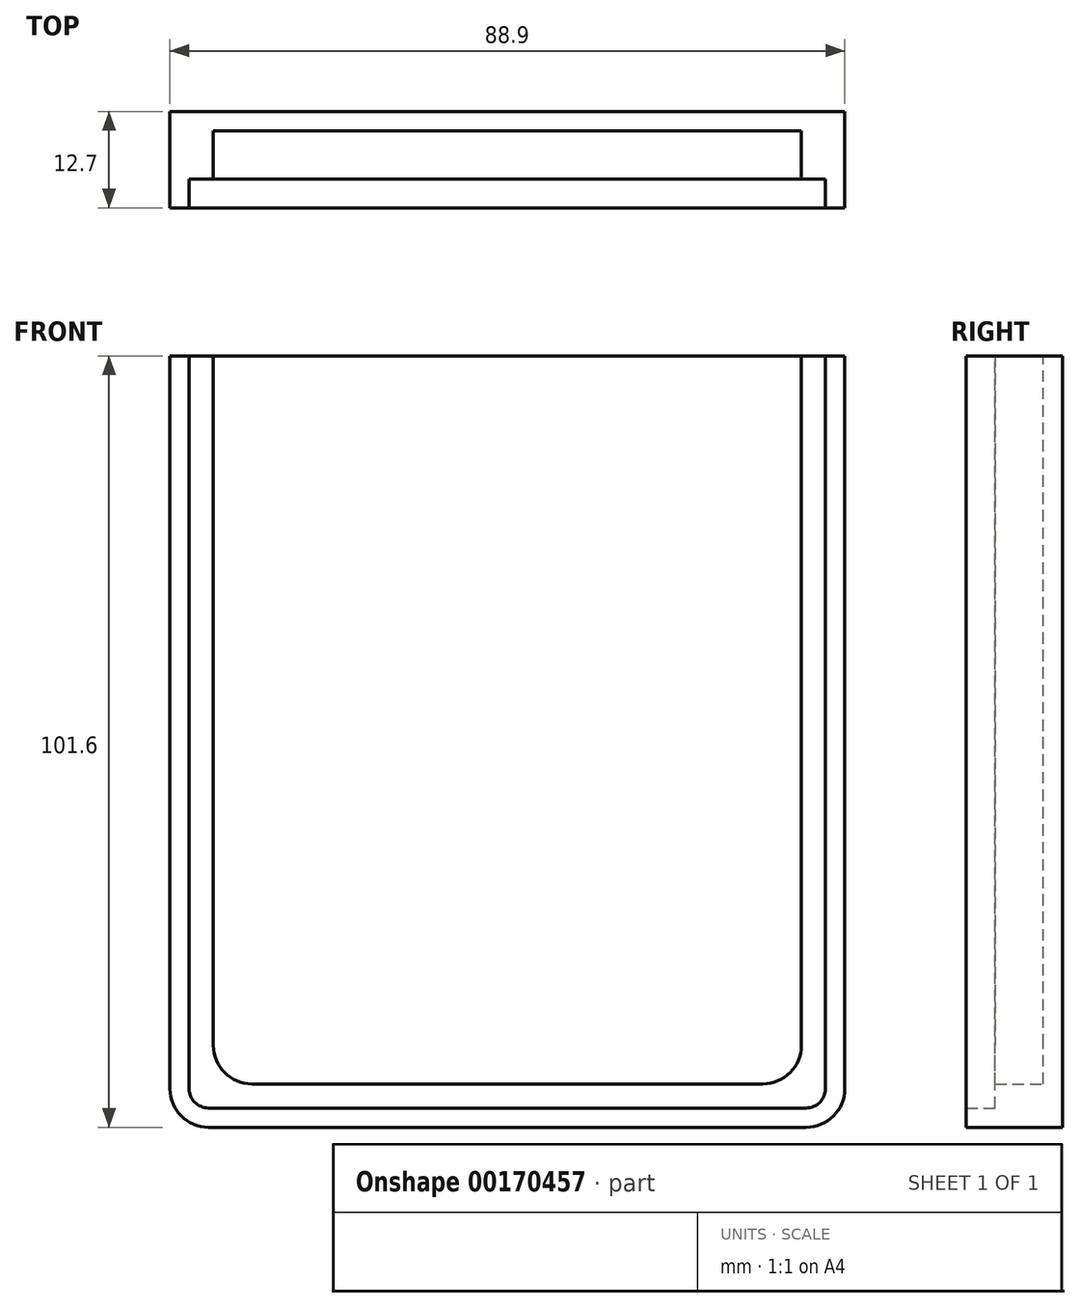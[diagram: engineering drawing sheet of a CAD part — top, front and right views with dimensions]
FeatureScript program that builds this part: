
annotation { "Feature Type Name" : "Feature", "Feature Type Description" : "" }
export const myFeature = defineFeature(function(context is Context, id is Id, definition is map)
    precondition{}
    {
        {
            var Q0;
            Q0=qCreatedBy(makeId("Front.planeOp"),FACE);
            var sketch = newSketch(context, id + "F0", { "sketchPlane" : qUnion([Q0])});
            skLineSegment(sketch, "E0.bottom", {"start": v(44.45, 0) * mm, "end": v(-44.45, 0) * mm});
            skLineSegment(sketch, "E0.top", {"start": v(44.45, 101.6) * mm, "end": v(-44.45, 101.6) * mm});
            skLineSegment(sketch, "E0.left", {"start": v(44.45, 0) * mm, "end": v(44.45, 101.6) * mm});
            skLineSegment(sketch, "E0.right", {"start": v(-44.45, 0) * mm, "end": v(-44.45, 101.6) * mm});
            skPoint(sketch, "E0.middle", {"position": v(0, 50.8) * mm});
            skLineSegment(sketch, "E1", {"start": v(0, 50.8) * mm, "end": v(0, 0) * mm, "construction": true});
            skSolve(sketch);
        }
        {
            var Q0;
            Q0=makeQuery(id+"F0.imprint","IMPRINT",FACE,{"disambiguationData":[TD([[makeQuery(id+"F0.imprint","IMPRINT",EDGE,{"derivedFrom":sQuery(id+"F0.wireOp",EDGE,"E0.bottom")}),-1.0]])]});
            extrude(context, id + "F1", {"entities" : qUnion([Q0]), "depth" : 12.7 * mm, "offsetDistance" : 25.4 * mm, "symmetric" : true});
        }
        {
            var Q0;
            Q0=makeQuery(id+"F1.opExtrude","SWEPT_EDGE",EDGE,{"disambiguationData":[OSD([sQuery(id+"F0.wireOp",EDGE,"E0.bottom"),sQuery(id+"F0.wireOp",EDGE,"E0.right")])]});
            var Q1;
            Q1=makeQuery(id+"F1.opExtrude","SWEPT_EDGE",EDGE,{"disambiguationData":[OSD([sQuery(id+"F0.wireOp",EDGE,"E0.bottom"),sQuery(id+"F0.wireOp",EDGE,"E0.left")])]});
            fillet(context, id + "F2", {"entities" : qUnion([Q0, Q1]), "radius" : 5.08 * mm, "tangentPropagation" : true, "allowEdgeOverflow" : false});
        }
        {
            var Q0;
            Q0=makeQuery(id+"F1.opExtrude","CAP_FACE",FACE,{"disambiguationData":[OSD([sQuery(id+"F0.wireOp",EDGE,"E0.bottom"),sQuery(id+"F0.wireOp",EDGE,"E0.top"),sQuery(id+"F0.wireOp",EDGE,"E0.left"),sQuery(id+"F0.wireOp",EDGE,"E0.right")])],"isStart":false});
            shell(context, id + "F3", {"entities" : qUnion([Q0]), "thickness" : 2.54 * mm});
        }
        {
            var Q0;
            Q0=makeQuery(id+"F1.opExtrude","CAP_FACE",FACE,{"disambiguationData":[OSD([sQuery(id+"F0.wireOp",EDGE,"E0.bottom"),sQuery(id+"F0.wireOp",EDGE,"E0.top"),sQuery(id+"F0.wireOp",EDGE,"E0.left"),sQuery(id+"F0.wireOp",EDGE,"E0.right")])],"isStart":false});
            var sketch = newSketch(context, id + "F4", { "sketchPlane" : qUnion([Q0])});
            skLineSegment(sketch, "E2.bottom", {"start": v(-41.9, 99.06) * mm, "end": v(41.91, 99.06) * mm});
            skLineSegment(sketch, "E2.top", {"start": v(-41.9, 101.6) * mm, "end": v(41.91, 101.6) * mm});
            skLineSegment(sketch, "E2.left", {"start": v(-41.9, 99.06) * mm, "end": v(-41.9, 101.6) * mm});
            skLineSegment(sketch, "E2.right", {"start": v(41.91, 99.06) * mm, "end": v(41.91, 101.6) * mm});
            skSolve(sketch);
        }
        {
            var Q0;
            Q0=makeQuery(id+"F4.imprint","IMPRINT",FACE,{"disambiguationData":[TD([[makeQuery(id+"F4.imprint","IMPRINT",EDGE,{"derivedFrom":sQuery(id+"F4.wireOp",EDGE,"E2.bottom")}),-1.0]])]});
            var Q1;
            Q1=makeQuery(id+"F3.opShell","OFFSET_FACE",FACE,{"disambiguationData":[OSD([sQuery(id+"F0.wireOp",EDGE,"E0.bottom"),sQuery(id+"F0.wireOp",EDGE,"E0.top"),sQuery(id+"F0.wireOp",EDGE,"E0.left"),sQuery(id+"F0.wireOp",EDGE,"E0.right")])]});
            extrude(context, id + "F5", {"entities" : qUnion([Q0]), "operationType" : NewBodyOperationType.REMOVE, "endBound" : BoundingType.UP_TO_SURFACE, "oppositeDirection" : true, "depth" : 25.4 * mm, "endBoundEntityFace" : qUnion([Q1]), "offsetDistance" : 25.4 * mm});
        }
        {
            var Q0;
            Q0=makeQuery(id+"F5.boolean.opBoolean","MERGE",FACE,{"derivedFrom":[makeQuery(id+"F3.opShell","OFFSET_FACE",FACE,{"disambiguationData":[OSD([sQuery(id+"F0.wireOp",EDGE,"E0.bottom"),sQuery(id+"F0.wireOp",EDGE,"E0.top"),sQuery(id+"F0.wireOp",EDGE,"E0.left"),sQuery(id+"F0.wireOp",EDGE,"E0.right")])]})],"fromTools":[makeQuery(id+"F5.opExtrude","CAP_FACE",FACE,{"disambiguationData":[OSD([sQuery(id+"F4.wireOp",EDGE,"E2.bottom"),sQuery(id+"F4.wireOp",EDGE,"E2.top"),sQuery(id+"F4.wireOp",EDGE,"E2.left"),sQuery(id+"F4.wireOp",EDGE,"E2.right")])],"isStart":false})]});
            var sketch = newSketch(context, id + "F6", { "sketchPlane" : qUnion([Q0])});
            skLineSegment(sketch, "E3.0", {"start": v(-38.74, 5.71) * mm, "end": v(38.74, 5.72) * mm});
            skLineSegment(sketch, "E3.1", {"start": v(-38.73, 101.6) * mm, "end": v(-38.74, 5.71) * mm});
            skLineSegment(sketch, "E3.3", {"start": v(38.74, 5.72) * mm, "end": v(38.74, 101.6) * mm});
            skLineSegment(sketch, "E4.0", {"start": v(-38.73, 101.6) * mm, "end": v(38.74, 101.6) * mm});
            skPoint(sketch, "E5.orphan", {"position": v(-41.9, 101.6) * mm});
            skPoint(sketch, "E6.orphan", {"position": v(41.91, 101.6) * mm});
            skSolve(sketch);
        }
        {
            var Q0;
            Q0=makeQuery(id+"F6.imprint","IMPRINT",FACE,{"disambiguationData":[TD([[makeQuery(id+"F6.imprint","IMPRINT",EDGE,{"derivedFrom":sQuery(id+"F6.wireOp",EDGE,"E3.0")}),-1.0]])]});
            extrude(context, id + "F7", {"entities" : qUnion([Q0]), "operationType" : NewBodyOperationType.ADD, "depth" : 6.35 * mm, "offsetDistance" : 25.4 * mm});
        }
        {
            var Q0;
            Q0=makeQuery(id+"F7.opExtrude","SWEPT_EDGE",EDGE,{"disambiguationData":[OSD([sQuery(id+"F6.wireOp",EDGE,"E3.0"),sQuery(id+"F6.wireOp",EDGE,"E3.1")])]});
            var Q1;
            Q1=makeQuery(id+"F7.opExtrude","SWEPT_EDGE",EDGE,{"disambiguationData":[OSD([sQuery(id+"F6.wireOp",EDGE,"E3.0"),sQuery(id+"F6.wireOp",EDGE,"E3.3")])]});
            fillet(context, id + "F8", {"entities" : qUnion([Q0, Q1]), "radius" : 5.08 * mm, "tangentPropagation" : true, "allowEdgeOverflow" : false});
        }
    });
